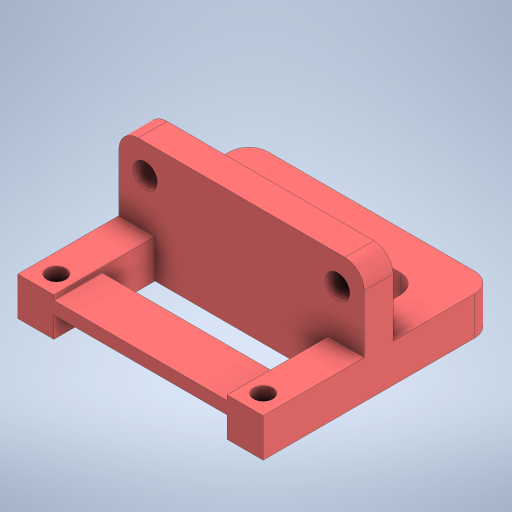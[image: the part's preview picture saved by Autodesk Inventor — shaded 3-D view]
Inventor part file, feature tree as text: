
AUTODESK INVENTOR PART (.ipt)
format: ipt  version: 2023 (Build 270158000, 158)  size: 415,232 bytes
history: native  units: mm
features: extrude x7, sketch x6, projected_geometry x3, other x2, fillet x2, chamfer x1
ambient origin geometry x8: Origin, YZ Plane, XZ Plane, XY Plane, X Axis, Y Axis, Z Axis, Center Point
bodies: Body1 (feature_tree)
feature tree (21):
  other  "솔리드1"
  sketch  "스케치1"
  extrude  "돌출1"  Depth=2.0mm
  extrude  "돌출2"  Depth=25.5mm
  fillet  "모깎기1"  Radius=24.0mm
  fillet  "모깎기4"  Radius=2.0mm
  other  "작업 평면1"
  extrude  "돌출5"  Depth=2.0mm
  chamfer  "모따기1"  Distance=18.0mm
  extrude  "돌출6"  Depth=20.0mm
  extrude  "돌출7"  Depth=5.0mm TaperAngle=0.0deg
  extrude  "돌출8"  Depth=10.0mm
  extrude  "돌출10"  Depth=10.5mm
  sketch  "스케치2"
  sketch  "스케치5"
  sketch  "스케치6"
  sketch  "스케치8"
  sketch  "스케치10"
  projected_geometry  "투영된 루프4"
  projected_geometry  "투영된 루프5"
  projected_geometry  "투영된 루프6"
